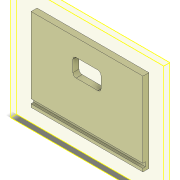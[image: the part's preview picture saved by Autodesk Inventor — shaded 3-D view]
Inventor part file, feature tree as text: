
AUTODESK INVENTOR PART (.ipt)
format: ipt  version: 2018.3 (Build 223284000, 284)  size: 187,392 bytes
history: native  units: in
note: dims shown in document units (in); Inventor stores cm internally (conversion verified against a paired STEP export)
features: extrude x3, sketch x3, fillet x1
ambient origin geometry x8: Origin, YZ Plane, XZ Plane, XY Plane, X Axis, Y Axis, Z Axis, Center Point
bodies: Solid1 (feature_tree)
feature tree (7):
  extrude  "Extrusion1"  Depth=2.19in
  extrude  "Extrusion2"  Depth=0.55in
  fillet  "Fillet1"  Radius=0.35in
  extrude  "Extrusion3"  Depth=0.938in
  sketch  "Sketch1"  dims[d0=1.625in d1=2.19in]
  sketch  "Sketch2"  dims[d2=0.118in d3=0.0in d4=0.55in d5=0.35in]
  sketch  "Sketch3"  dims[d6=0.82in d7=0.938in d8=0.118in d9=0.0in d10=0.0625in d11=0.0625in d12=0.085in d13=0.049in d14=0.0in]
